# Revit family: EQ
name_source: partatom
category: Wyposażenie mechaniczne
revit_build: Autodesk Revit 2017 (Build: 20160225_1515(x64)
units: mm (PartAtom-declared; Revit-internal decimal feet)

## family parameters
Oparty na płaszczyźnie roboczej = Nie
Punkt obliczania pomieszczeń = Nie
Tnij formami wycięć po wczytaniu = Nie
Typ części = Normalny
Współdzielony = Nie
Wymiar okrągłego złącza = Użyj średnicy
Zawsze pionowo = Tak

## types (27) — shared parameters
Date = 01.2019
Frequency = 50 Hz
Producent = Rosenberg
URL = https://www.rosenberg.pl
Version = 1
Voltage = 230 V

## per-type parameters (varying)
- 400-4.4EC: 200_cover=Nie; 250_cover=Nie; 300_cover=Nie; 350_cover=Nie; 400_cover=Tak; 450_cover=Nie; 500_cover=Nie; 560_cover=Nie; 630_cover=Nie; 710_cover=Nie; Air_flow=3245.0 m³/h; Current=1 A; Electrical_motor_diameter=30 mm  [stored 0.0984252 ft]; Electrical_motor_length_back=60 mm  [stored 0.19685 ft]; Electrical_motor_length_front=50 mm  [stored 0.164042 ft]; Housing_dimension=540 mm; Housing_dimension/2=270 mm; Inner_diameter=403 mm; Outer_diameter=437 mm; Power=0 kW; Pressure=67.0 Pa; Propeller_length=197 mm; Protection_class=IP54; Radius_inner=202 mm; Radius_outer=219 mm; Sheet_metal_thickness=12 mm  [stored 0.0393701 ft]; Thickness=88 mm  [stored 0.288714 ft]; Weight=7.70 kg; max.Ambient_temperature=60 °C
- 250-2.3CF: 200_cover=Nie; 250_cover=Tak; 300_cover=Nie; 350_cover=Nie; 400_cover=Nie; 450_cover=Nie; 500_cover=Nie; 560_cover=Nie; 630_cover=Nie; 710_cover=Nie; Air_flow=0.0 m³/h; Current=1 A; Electrical_motor_diameter=30 mm  [stored 0.0984252 ft]; Electrical_motor_length_back=85 mm  [stored 0.278871 ft]; Electrical_motor_length_front=8 mm  [stored 0.0262467 ft]; Housing_dimension=370 mm; Housing_dimension/2=185 mm; Inner_diameter=254 mm; Outer_diameter=275 mm; Power=0 kW; Pressure=0.0 Pa; Propeller_length=122 mm; Protection_class=IP44; Radius_inner=127 mm; Radius_outer=138 mm; Sheet_metal_thickness=6 mm  [stored 0.019685 ft]; Thickness=78 mm  [stored 0.255906 ft]; Weight=3.50 kg; max.Ambient_temperature=60 °C
- 200-2.3BF: 200_cover=Tak; 250_cover=Nie; 300_cover=Nie; 350_cover=Nie; 400_cover=Nie; 450_cover=Nie; 500_cover=Nie; 560_cover=Nie; 630_cover=Nie; 710_cover=Nie; Air_flow=0.0 m³/h; Current=0 A; Electrical_motor_diameter=30 mm  [stored 0.0984252 ft]; Electrical_motor_length_back=61 mm  [stored 0.200131 ft]; Electrical_motor_length_front=15 mm  [stored 0.0492126 ft]; Housing_dimension=312 mm; Housing_dimension/2=156 mm  [stored 0.511811 ft]; Inner_diameter=204 mm; Outer_diameter=215 mm; Power=0 kW; Pressure=0.0 Pa; Propeller_length=97 mm; Protection_class=IP44; Radius_inner=102 mm; Radius_outer=108 mm; Sheet_metal_thickness=6 mm  [stored 0.019685 ft]; Thickness=64 mm  [stored 0.209974 ft]; Weight=2.50 kg; max.Ambient_temperature=70 °C
- 300-2.3EF: 200_cover=Nie; 250_cover=Nie; 300_cover=Tak; 350_cover=Nie; 400_cover=Nie; 450_cover=Nie; 500_cover=Nie; 560_cover=Nie; 630_cover=Nie; 710_cover=Nie; Air_flow=0.0 m³/h; Current=1 A; Electrical_motor_diameter=30 mm  [stored 0.0984252 ft]; Electrical_motor_length_back=60 mm  [stored 0.19685 ft]; Electrical_motor_length_front=5 mm  [stored 0.0164042 ft]; Housing_dimension=430 mm; Housing_dimension/2=215 mm; Inner_diameter=305 mm; Outer_diameter=332 mm; Power=0 kW; Pressure=0.0 Pa; Propeller_length=148 mm  [stored 0.485564 ft]; Protection_class=IP44; Radius_inner=153 mm; Radius_outer=166 mm; Sheet_metal_thickness=11 mm  [stored 0.0360892 ft]; Thickness=100 mm  [stored 0.328084 ft]; Weight=6.00 kg; max.Ambient_temperature=55 °C
- 350-2: 200_cover=Nie; 250_cover=Nie; 300_cover=Nie; 350_cover=Tak; 400_cover=Nie; 450_cover=Nie; 500_cover=Nie; 560_cover=Nie; 630_cover=Nie; 710_cover=Nie; Air_flow=3738.0 m³/h; Current=4 A; Electrical_motor_diameter=30 mm  [stored 0.0984252 ft]; Electrical_motor_length_back=60 mm  [stored 0.19685 ft]; Electrical_motor_length_front=41 mm  [stored 0.134514 ft]; Housing_dimension=485 mm; Housing_dimension/2=243 mm; Inner_diameter=358 mm; Outer_diameter=381 mm; Power=1 kW; Pressure=217.0 Pa; Propeller_length=174 mm; Protection_class=IP54; Radius_inner=179 mm; Radius_outer=191 mm; Sheet_metal_thickness=12 mm  [stored 0.0393701 ft]; Thickness=74 mm  [stored 0.242782 ft]; Weight=13.00 kg; max.Ambient_temperature=40 °C
- 200-4.3BF: 200_cover=Tak; 250_cover=Nie; 300_cover=Nie; 350_cover=Nie; 400_cover=Nie; 450_cover=Nie; 500_cover=Nie; 560_cover=Nie; 630_cover=Nie; 710_cover=Nie; Air_flow=0.0 m³/h; Current=0 A; Electrical_motor_diameter=30 mm  [stored 0.0984252 ft]; Electrical_motor_length_back=61 mm  [stored 0.200131 ft]; Electrical_motor_length_front=15 mm  [stored 0.0492126 ft]; Housing_dimension=312 mm; Housing_dimension/2=156 mm  [stored 0.511811 ft]; Inner_diameter=204 mm; Outer_diameter=215 mm; Power=0 kW; Pressure=0.0 Pa; Propeller_length=97 mm; Protection_class=IP44; Radius_inner=102 mm; Radius_outer=108 mm; Sheet_metal_thickness=6 mm  [stored 0.019685 ft]; Thickness=68 mm; Weight=2.50 kg; max.Ambient_temperature=70 °C
- 250-4.3CF: 200_cover=Nie; 250_cover=Tak; 300_cover=Nie; 350_cover=Nie; 400_cover=Nie; 450_cover=Nie; 500_cover=Nie; 560_cover=Nie; 630_cover=Nie; 710_cover=Nie; Air_flow=0.0 m³/h; Current=0 A; Electrical_motor_diameter=30 mm  [stored 0.0984252 ft]; Electrical_motor_length_back=85 mm  [stored 0.278871 ft]; Electrical_motor_length_front=8 mm  [stored 0.0262467 ft]; Housing_dimension=370 mm; Housing_dimension/2=185 mm; Inner_diameter=254 mm; Outer_diameter=275 mm; Power=0 kW; Pressure=0.0 Pa; Propeller_length=122 mm; Protection_class=IP44; Radius_inner=127 mm; Radius_outer=138 mm; Sheet_metal_thickness=6 mm  [stored 0.019685 ft]; Thickness=78 mm  [stored 0.255906 ft]; Weight=4.00 kg; max.Ambient_temperature=70 °C
- 300-4.3DF: 200_cover=Nie; 250_cover=Nie; 300_cover=Tak; 350_cover=Nie; 400_cover=Nie; 450_cover=Nie; 500_cover=Nie; 560_cover=Nie; 630_cover=Nie; 710_cover=Nie; Air_flow=0.0 m³/h; Current=0 A; Electrical_motor_diameter=30 mm  [stored 0.0984252 ft]; Electrical_motor_length_back=60 mm  [stored 0.19685 ft]; Electrical_motor_length_front=5 mm  [stored 0.0164042 ft]; Housing_dimension=430 mm; Housing_dimension/2=215 mm; Inner_diameter=305 mm; Outer_diameter=332 mm; Power=0 kW; Pressure=0.0 Pa; Propeller_length=148 mm  [stored 0.485564 ft]; Protection_class=IP44; Radius_inner=153 mm; Radius_outer=166 mm; Sheet_metal_thickness=11 mm  [stored 0.0360892 ft]; Thickness=90 mm  [stored 0.295276 ft]; Weight=6.00 kg; max.Ambient_temperature=55 °C
- 315-2: 200_cover=Nie; 250_cover=Nie; 300_cover=Tak; 350_cover=Nie; 400_cover=Nie; 450_cover=Nie; 500_cover=Nie; 560_cover=Nie; 630_cover=Nie; 710_cover=Nie; Air_flow=2796.0 m³/h; Current=3 A; Electrical_motor_diameter=30 mm  [stored 0.0984252 ft]; Electrical_motor_length_back=60 mm  [stored 0.19685 ft]; Electrical_motor_length_front=5 mm  [stored 0.0164042 ft]; Housing_dimension=430 mm; Housing_dimension/2=215 mm; Inner_diameter=317 mm; Outer_diameter=330 mm; Power=1 kW; Pressure=208.0 Pa; Propeller_length=154 mm; Protection_class=IP54; Radius_inner=159 mm; Radius_outer=165 mm; Sheet_metal_thickness=11 mm  [stored 0.0360892 ft]; Thickness=71 mm  [stored 0.23294 ft]; Weight=10.40 kg; max.Ambient_temperature=50 °C
- 315-2.4FF: 200_cover=Nie; 250_cover=Nie; 300_cover=Tak; 350_cover=Nie; 400_cover=Nie; 450_cover=Nie; 500_cover=Nie; 560_cover=Nie; 630_cover=Nie; 710_cover=Nie; Air_flow=2499.0 m³/h; Current=2 A; Electrical_motor_diameter=30 mm  [stored 0.0984252 ft]; Electrical_motor_length_back=60 mm  [stored 0.19685 ft]; Electrical_motor_length_front=5 mm  [stored 0.0164042 ft]; Housing_dimension=430 mm; Housing_dimension/2=215 mm; Inner_diameter=317 mm; Outer_diameter=330 mm; Power=0 kW; Pressure=168.0 Pa; Propeller_length=154 mm; Protection_class=IP54; Radius_inner=159 mm; Radius_outer=165 mm; Sheet_metal_thickness=11 mm  [stored 0.0360892 ft]; Thickness=71 mm  [stored 0.23294 ft]; Weight=5.50 kg; max.Ambient_temperature=50 °C
- 315-4.4DA: 200_cover=Nie; 250_cover=Nie; 300_cover=Tak; 350_cover=Nie; 400_cover=Nie; 450_cover=Nie; 500_cover=Nie; 560_cover=Nie; 630_cover=Nie; 710_cover=Nie; Air_flow=0.0 m³/h; Current=1 A; Electrical_motor_diameter=30 mm  [stored 0.0984252 ft]; Electrical_motor_length_back=60 mm  [stored 0.19685 ft]; Electrical_motor_length_front=5 mm  [stored 0.0164042 ft]; Housing_dimension=430 mm; Housing_dimension/2=215 mm; Inner_diameter=317 mm; Outer_diameter=330 mm; Power=0 kW; Pressure=0.0 Pa; Propeller_length=154 mm; Protection_class=IP54; Radius_inner=159 mm; Radius_outer=165 mm; Sheet_metal_thickness=11 mm  [stored 0.0360892 ft]; Thickness=71 mm  [stored 0.23294 ft]; Weight=6.00 kg; max.Ambient_temperature=65 °C
- 315-6.4DA: 200_cover=Nie; 250_cover=Nie; 300_cover=Tak; 350_cover=Nie; 400_cover=Nie; 450_cover=Nie; 500_cover=Nie; 560_cover=Nie; 630_cover=Nie; 710_cover=Nie; Air_flow=0.0 m³/h; Current=0 A; Electrical_motor_diameter=30 mm  [stored 0.0984252 ft]; Electrical_motor_length_back=60 mm  [stored 0.19685 ft]; Electrical_motor_length_front=5 mm  [stored 0.0164042 ft]; Housing_dimension=430 mm; Housing_dimension/2=215 mm; Inner_diameter=317 mm; Outer_diameter=330 mm; Power=0 kW; Pressure=0.0 Pa; Propeller_length=154 mm; Protection_class=IP54; Radius_inner=159 mm; Radius_outer=165 mm; Sheet_metal_thickness=11 mm  [stored 0.0360892 ft]; Thickness=71 mm  [stored 0.23294 ft]; Weight=6.50 kg; max.Ambient_temperature=60 °C
- 350-4: 200_cover=Nie; 250_cover=Nie; 300_cover=Nie; 350_cover=Tak; 400_cover=Nie; 450_cover=Nie; 500_cover=Nie; 560_cover=Nie; 630_cover=Nie; 710_cover=Nie; Air_flow=2255.0 m³/h; Current=1 A; Electrical_motor_diameter=30 mm  [stored 0.0984252 ft]; Electrical_motor_length_back=60 mm  [stored 0.19685 ft]; Electrical_motor_length_front=41 mm  [stored 0.134514 ft]; Housing_dimension=485 mm; Housing_dimension/2=243 mm; Inner_diameter=358 mm; Outer_diameter=381 mm; Power=0 kW; Pressure=57.0 Pa; Propeller_length=174 mm; Protection_class=IP54; Radius_inner=179 mm; Radius_outer=191 mm; Sheet_metal_thickness=12 mm  [stored 0.0393701 ft]; Thickness=74 mm  [stored 0.242782 ft]; Weight=7.00 kg; max.Ambient_temperature=65 °C
- 350-4.4EC: 200_cover=Nie; 250_cover=Nie; 300_cover=Nie; 350_cover=Tak; 400_cover=Nie; 450_cover=Nie; 500_cover=Nie; 560_cover=Nie; 630_cover=Nie; 710_cover=Nie; Air_flow=2150.0 m³/h; Current=1 A; Electrical_motor_diameter=30 mm  [stored 0.0984252 ft]; Electrical_motor_length_back=60 mm  [stored 0.19685 ft]; Electrical_motor_length_front=41 mm  [stored 0.134514 ft]; Housing_dimension=485 mm; Housing_dimension/2=243 mm; Inner_diameter=358 mm; Outer_diameter=381 mm; Power=0 kW; Pressure=78.0 Pa; Propeller_length=174 mm; Protection_class=IP54; Radius_inner=179 mm; Radius_outer=191 mm; Sheet_metal_thickness=12 mm  [stored 0.0393701 ft]; Thickness=74 mm  [stored 0.242782 ft]; Weight=7.50 kg; max.Ambient_temperature=70 °C
- 350-6.4DA: 200_cover=Nie; 250_cover=Nie; 300_cover=Nie; 350_cover=Tak; 400_cover=Nie; 450_cover=Nie; 500_cover=Nie; 560_cover=Nie; 630_cover=Nie; 710_cover=Nie; Air_flow=0.0 m³/h; Current=0 A; Electrical_motor_diameter=40 mm  [stored 0.131234 ft]; Electrical_motor_length_back=60 mm  [stored 0.19685 ft]; Electrical_motor_length_front=50 mm  [stored 0.164042 ft]; Housing_dimension=485 mm; Housing_dimension/2=243 mm; Inner_diameter=358 mm; Outer_diameter=381 mm; Power=0 kW; Pressure=0.0 Pa; Propeller_length=174 mm; Protection_class=IP54; Radius_inner=179 mm; Radius_outer=191 mm; Sheet_metal_thickness=12 mm  [stored 0.0393701 ft]; Thickness=74 mm  [stored 0.242782 ft]; Weight=8.00 kg; max.Ambient_temperature=60 °C
- 400-6.4DA: 200_cover=Nie; 250_cover=Nie; 300_cover=Nie; 350_cover=Nie; 400_cover=Tak; 450_cover=Nie; 500_cover=Nie; 560_cover=Nie; 630_cover=Nie; 710_cover=Nie; Air_flow=0.0 m³/h; Current=0 A; Electrical_motor_diameter=65 mm  [stored 0.213255 ft]; Electrical_motor_length_back=60 mm  [stored 0.19685 ft]; Electrical_motor_length_front=50 mm  [stored 0.164042 ft]; Housing_dimension=540 mm; Housing_dimension/2=270 mm; Inner_diameter=403 mm; Outer_diameter=437 mm; Power=0 kW; Pressure=0.0 Pa; Propeller_length=197 mm; Protection_class=IP54; Radius_inner=202 mm; Radius_outer=219 mm; Sheet_metal_thickness=12 mm  [stored 0.0393701 ft]; Thickness=88 mm  [stored 0.288714 ft]; Weight=7.00 kg; max.Ambient_temperature=55 °C
- 450-4.5DF: 200_cover=Nie; 250_cover=Nie; 300_cover=Nie; 350_cover=Nie; 400_cover=Nie; 450_cover=Tak; 500_cover=Nie; 560_cover=Nie; 630_cover=Nie; 710_cover=Nie; Air_flow=4055.0 m³/h; Current=1 A; Electrical_motor_diameter=65 mm  [stored 0.213255 ft]; Electrical_motor_length_back=60 mm  [stored 0.19685 ft]; Electrical_motor_length_front=50 mm  [stored 0.164042 ft]; Housing_dimension=575 mm; Housing_dimension/2=288 mm; Inner_diameter=452 mm; Outer_diameter=513 mm; Power=0 kW; Pressure=92.0 Pa; Propeller_length=221 mm; Protection_class=IP54; Radius_inner=226 mm; Radius_outer=257 mm; Sheet_metal_thickness=14 mm  [stored 0.0459318 ft]; Thickness=86 mm  [stored 0.282152 ft]; Weight=11.00 kg; max.Ambient_temperature=55 °C
- 450-6.5DF: 200_cover=Nie; 250_cover=Nie; 300_cover=Nie; 350_cover=Nie; 400_cover=Nie; 450_cover=Tak; 500_cover=Nie; 560_cover=Nie; 630_cover=Nie; 710_cover=Nie; Air_flow=0.0 m³/h; Current=1 A; Electrical_motor_diameter=65 mm  [stored 0.213255 ft]; Electrical_motor_length_back=60 mm  [stored 0.19685 ft]; Electrical_motor_length_front=50 mm  [stored 0.164042 ft]; Housing_dimension=575 mm; Housing_dimension/2=288 mm; Inner_diameter=452 mm; Outer_diameter=513 mm; Power=0 kW; Pressure=0.0 Pa; Propeller_length=221 mm; Protection_class=IP54; Radius_inner=226 mm; Radius_outer=257 mm; Sheet_metal_thickness=14 mm  [stored 0.0459318 ft]; Thickness=86 mm  [stored 0.282152 ft]; Weight=10.50 kg; max.Ambient_temperature=70 °C
- 500-4.5FA: 200_cover=Nie; 250_cover=Nie; 300_cover=Nie; 350_cover=Nie; 400_cover=Nie; 450_cover=Nie; 500_cover=Tak; 560_cover=Nie; 630_cover=Nie; 710_cover=Nie; Air_flow=5483.0 m³/h; Current=2 A; Electrical_motor_diameter=65 mm  [stored 0.213255 ft]; Electrical_motor_length_back=60 mm  [stored 0.19685 ft]; Electrical_motor_length_front=50 mm  [stored 0.164042 ft]; Housing_dimension=655 mm; Housing_dimension/2=328 mm; Inner_diameter=504 mm; Outer_diameter=540 mm; Power=0 kW; Pressure=108.0 Pa; Propeller_length=247 mm; Protection_class=IP54; Radius_inner=252 mm; Radius_outer=270 mm; Sheet_metal_thickness=16 mm  [stored 0.0524934 ft]; Thickness=104 mm  [stored 0.341207 ft]; Weight=15.00 kg; max.Ambient_temperature=50 °C
- 500-6: 200_cover=Nie; 250_cover=Nie; 300_cover=Nie; 350_cover=Nie; 400_cover=Nie; 450_cover=Nie; 500_cover=Tak; 560_cover=Nie; 630_cover=Nie; 710_cover=Nie; Air_flow=3652.0 m³/h; Current=1 A; Electrical_motor_diameter=65 mm  [stored 0.213255 ft]; Electrical_motor_length_back=60 mm  [stored 0.19685 ft]; Electrical_motor_length_front=50 mm  [stored 0.164042 ft]; Housing_dimension=655 mm; Housing_dimension/2=328 mm; Inner_diameter=504 mm; Outer_diameter=540 mm; Power=0 kW; Pressure=49.0 Pa; Propeller_length=247 mm; Protection_class=IP54; Radius_inner=252 mm; Radius_outer=270 mm; Sheet_metal_thickness=16 mm  [stored 0.0524934 ft]; Thickness=104 mm  [stored 0.341207 ft]; Weight=15.00 kg; max.Ambient_temperature=60 °C
- 560-4: 200_cover=Nie; 250_cover=Nie; 300_cover=Nie; 350_cover=Nie; 400_cover=Nie; 450_cover=Nie; 500_cover=Nie; 560_cover=Tak; 630_cover=Nie; 710_cover=Nie; Air_flow=7173.0 m³/h; Current=4 A; Electrical_motor_diameter=65 mm  [stored 0.213255 ft]; Electrical_motor_length_back=60 mm  [stored 0.19685 ft]; Electrical_motor_length_front=50 mm  [stored 0.164042 ft]; Housing_dimension=725 mm; Housing_dimension/2=363 mm; Inner_diameter=560 mm; Outer_diameter=597 mm; Power=1 kW; Pressure=124.0 Pa; Propeller_length=275 mm; Protection_class=IP54; Radius_inner=280 mm; Radius_outer=299 mm; Sheet_metal_thickness=16 mm  [stored 0.0524934 ft]; Thickness=104 mm  [stored 0.341207 ft]; Weight=19.00 kg; max.Ambient_temperature=40 °C
- 560-4(6HF): 200_cover=Nie; 250_cover=Nie; 300_cover=Nie; 350_cover=Nie; 400_cover=Nie; 450_cover=Nie; 500_cover=Nie; 560_cover=Tak; 630_cover=Nie; 710_cover=Nie; Air_flow=8171.0 m³/h; Current=6 A; Electrical_motor_diameter=65 mm  [stored 0.213255 ft]; Electrical_motor_length_back=60 mm  [stored 0.19685 ft]; Electrical_motor_length_front=50 mm  [stored 0.164042 ft]; Housing_dimension=725 mm; Housing_dimension/2=363 mm; Inner_diameter=560 mm; Outer_diameter=597 mm; Power=1 kW; Pressure=150.0 Pa; Propeller_length=275 mm; Protection_class=IP54; Radius_inner=280 mm; Radius_outer=299 mm; Sheet_metal_thickness=16 mm  [stored 0.0524934 ft]; Thickness=104 mm  [stored 0.341207 ft]; Weight=27.60 kg; max.Ambient_temperature=60 °C
- 560-4.5HA: 200_cover=Nie; 250_cover=Nie; 300_cover=Nie; 350_cover=Nie; 400_cover=Nie; 450_cover=Nie; 500_cover=Nie; 560_cover=Tak; 630_cover=Nie; 710_cover=Nie; Air_flow=8442.0 m³/h; Current=4 A; Electrical_motor_diameter=65 mm  [stored 0.213255 ft]; Electrical_motor_length_back=60 mm  [stored 0.19685 ft]; Electrical_motor_length_front=50 mm  [stored 0.164042 ft]; Housing_dimension=725 mm; Housing_dimension/2=363 mm; Inner_diameter=560 mm; Outer_diameter=597 mm; Power=1 kW; Pressure=134.0 Pa; Propeller_length=275 mm; Protection_class=IP54; Radius_inner=280 mm; Radius_outer=299 mm; Sheet_metal_thickness=16 mm  [stored 0.0524934 ft]; Thickness=104 mm  [stored 0.341207 ft]; Weight=19.00 kg; max.Ambient_temperature=40 °C
- 560-6.5FA: 200_cover=Nie; 250_cover=Nie; 300_cover=Nie; 350_cover=Nie; 400_cover=Nie; 450_cover=Nie; 500_cover=Nie; 560_cover=Tak; 630_cover=Nie; 710_cover=Nie; Air_flow=5680.0 m³/h; Current=2 A; Electrical_motor_diameter=65 mm  [stored 0.213255 ft]; Electrical_motor_length_back=60 mm  [stored 0.19685 ft]; Electrical_motor_length_front=50 mm  [stored 0.164042 ft]; Housing_dimension=725 mm; Housing_dimension/2=363 mm; Inner_diameter=560 mm; Outer_diameter=597 mm; Power=0 kW; Pressure=65.0 Pa; Propeller_length=275 mm; Protection_class=IP54; Radius_inner=280 mm; Radius_outer=299 mm; Sheet_metal_thickness=16 mm  [stored 0.0524934 ft]; Thickness=104 mm  [stored 0.341207 ft]; Weight=17.00 kg; max.Ambient_temperature=60 °C
- 630-4: 200_cover=Nie; 250_cover=Nie; 300_cover=Nie; 350_cover=Nie; 400_cover=Nie; 450_cover=Nie; 500_cover=Nie; 560_cover=Nie; 630_cover=Tak; 710_cover=Nie; Air_flow=12288.0 m³/h; Current=10 A; Electrical_motor_diameter=65 mm  [stored 0.213255 ft]; Electrical_motor_length_back=60 mm  [stored 0.19685 ft]; Electrical_motor_length_front=50 mm  [stored 0.164042 ft]; Housing_dimension=805 mm; Housing_dimension/2=403 mm; Inner_diameter=635 mm; Outer_diameter=683 mm; Power=2 kW; Pressure=204.0 Pa; Propeller_length=313 mm; Protection_class=IP54; Radius_inner=318 mm; Radius_outer=342 mm; Sheet_metal_thickness=20 mm  [stored 0.0656168 ft]; Thickness=130 mm  [stored 0.426509 ft]; Weight=36.00 kg; max.Ambient_temperature=40 °C
- 630-6.5HA: 200_cover=Nie; 250_cover=Nie; 300_cover=Nie; 350_cover=Nie; 400_cover=Nie; 450_cover=Nie; 500_cover=Nie; 560_cover=Nie; 630_cover=Tak; 710_cover=Nie; Air_flow=7647.0 m³/h; Current=2 A; Electrical_motor_diameter=65 mm  [stored 0.213255 ft]; Electrical_motor_length_back=60 mm  [stored 0.19685 ft]; Electrical_motor_length_front=50 mm  [stored 0.164042 ft]; Housing_dimension=805 mm; Housing_dimension/2=403 mm; Inner_diameter=635 mm; Outer_diameter=683 mm; Power=0 kW; Pressure=70.0 Pa; Propeller_length=313 mm; Protection_class=IP54; Radius_inner=318 mm; Radius_outer=342 mm; Sheet_metal_thickness=20 mm  [stored 0.0656168 ft]; Thickness=130 mm  [stored 0.426509 ft]; Weight=21.30 kg; max.Ambient_temperature=60 °C
- 710-6: 200_cover=Nie; 250_cover=Nie; 300_cover=Nie; 350_cover=Nie; 400_cover=Nie; 450_cover=Nie; 500_cover=Nie; 560_cover=Nie; 630_cover=Nie; 710_cover=Tak; Air_flow=10468.0 m³/h; Current=5 A; Electrical_motor_diameter=50 mm  [stored 0.164042 ft]; Electrical_motor_length_back=60 mm  [stored 0.19685 ft]; Electrical_motor_length_front=50 mm  [stored 0.164042 ft]; Housing_dimension=850 mm; Housing_dimension/2=425 mm; Inner_diameter=711 mm; Outer_diameter=772 mm; Power=1 kW; Pressure=94.0 Pa; Propeller_length=351 mm; Protection_class=IP54; Radius_inner=356 mm; Radius_outer=386 mm; Sheet_metal_thickness=20 mm  [stored 0.0656168 ft]; Thickness=150 mm; Weight=38.00 kg; max.Ambient_temperature=70 °C

note: column(s) folded — value = type name in every type: Model

note: [stored X ft] marks values corroborated as IEEE doubles in the binary element streams (Revit-internal decimal feet)
